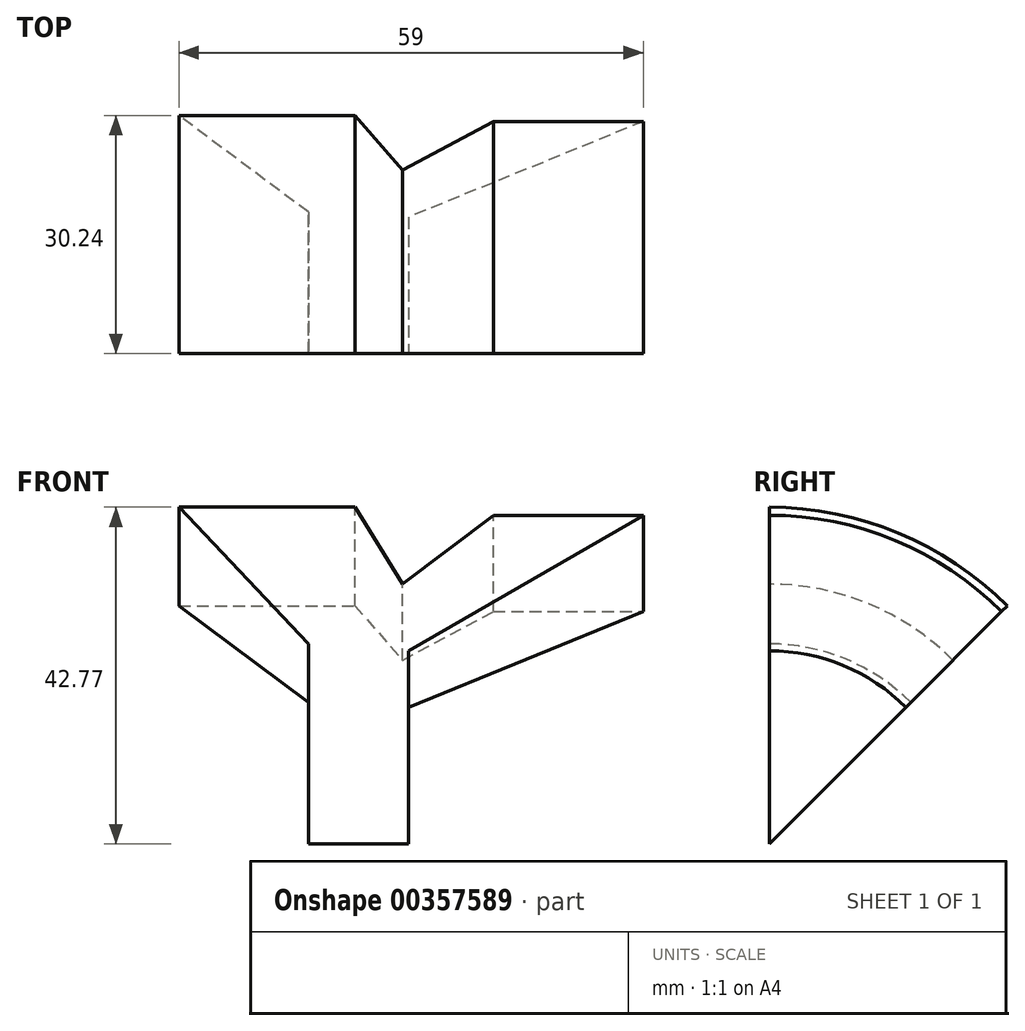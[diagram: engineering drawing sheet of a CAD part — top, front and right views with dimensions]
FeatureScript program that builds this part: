
annotation { "Feature Type Name" : "Feature", "Feature Type Description" : "" }
export const myFeature = defineFeature(function(context is Context, id is Id, definition is map)
    precondition{}
    {
        {
            var Q0;
            Q0=qCreatedBy(makeId("Front.planeOp"),FACE);
            var sketch = newSketch(context, id + "F0", { "sketchPlane" : qUnion([Q0])});
            skLineSegment(sketch, "E0", {"start": v(0, 0) * mm, "end": v(0, 25.4) * mm});
            skLineSegment(sketch, "E1", {"start": v(0, 25.4) * mm, "end": v(-16.5, 42.77) * mm});
            skLineSegment(sketch, "E2", {"start": v(-16.5, 42.77) * mm, "end": v(5.86, 42.77) * mm});
            skLineSegment(sketch, "E3", {"start": v(5.86, 42.77) * mm, "end": v(11.94, 33) * mm});
            skLineSegment(sketch, "E4", {"start": v(11.94, 33) * mm, "end": v(23.45, 41.74) * mm});
            skLineSegment(sketch, "E5", {"start": v(23.45, 41.74) * mm, "end": v(42.5, 41.74) * mm});
            skLineSegment(sketch, "E6", {"start": v(42.5, 41.74) * mm, "end": v(12.7, 24.53) * mm});
            skLineSegment(sketch, "E7", {"start": v(12.7, 24.53) * mm, "end": v(12.7, 0) * mm});
            skLineSegment(sketch, "E8", {"start": v(12.7, 0) * mm, "end": v(0, 0) * mm});
            skSolve(sketch);
        }
        {
            var Q0;
            Q0=makeQuery(id+"F0.imprint","IMPRINT",FACE,{"disambiguationData":[TD([[makeQuery(id+"F0.imprint","IMPRINT",EDGE,{"derivedFrom":sQuery(id+"F0.wireOp",EDGE,"E0")}),-1.0]])]});
            var Q1;
            Q1=sQuery(id+"F0.wireOp",EDGE,"E8");
            revolve(context, id + "F1", {"entities" : qUnion([Q0]), "axis" : qUnion([Q1]), "revolveType" : RevolveType.ONE_DIRECTION, "angle" : 45 * degree});
        }
    });
